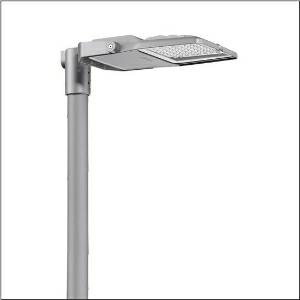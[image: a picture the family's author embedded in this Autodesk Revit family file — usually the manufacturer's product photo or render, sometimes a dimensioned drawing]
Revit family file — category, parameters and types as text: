
# Revit family: floodlight_fl_21_iq_mini___pl61_5xa7772b2c3a_0206
name_source: partatom
category: Lighting Fixtures
units: mm (PartAtom-declared; Revit-internal decimal feet)

## family parameters
Cut with Voids When Loaded = No
Host = Face
Light Source = No
Part Type = Normal
Room Calculation Point = No
Round Connector Dimension = Use Diameter
Shared = No

## types (1)
- --- (1 x LED, 6120 lm, 45.5 W, 3000K)
    Apparent Load = 46 VA
    CIE Flux Codes = 33 65 98 100 100
    Color Rendering = 70
    Color Temperature = 3000K
    Default Elevation = 1800 mm
    Description = Floodlight FL 21 iQ mini, floodlight, primary light control with lens, of PMMA, primary optical cover: protective disc, of toughened safety glass, transparent, light distribution: PL61, light emission: direct distribution, installation type: surface-mounted, LED, High Power LED, rated luminous flux: 6.120lm, luminous efficacy: 135lm/W, light colour: 730, colour temperature: 3000K, control gear: iQ Street-Remote/DALI, control: Auto-Match, Temp-Guard, Night-Set, Smart-Wire, Desk-Remote (wireless, voltage-free reading and setting of iQ features in the workshop via application-optimized NFC function/RFID function), optimised constant luminous flux control (CLO 2.0), Light-Fading, Lumen-Switch, with terminal, 6-pole, mains connection: 220..240V, AC, 50/60Hz, start of lifetime: 46W, end of service life: 48W, reduction: 22W, luminaire housing, of diecast aluminium, powder-coated, Siteco® metallic grey (DB 702S), corrosivity category C5 mid according to DIN EN ISO 12944, suitable for swimming pools, chlorine-resistant, sealing non-destructively replaceable, please order mast flange separately, mast bracket, of steel, galvanised, powder-coated, protection rating (complete): IP66, insulation class (complete): insulation class II (safety insulation), certification: CE, ENEC, VDE, protection symbol: D, impact resistance: IK08, permissible operating ambient temperature: -40..+40°C, permissible operating ambient temperature for outdoor applications: -40..+50°C, standard: DIN EN 12944, LABS conformity tested according to VDMA 24364:2018-05, packaging unit: 1 piece

Light Distribution: PL61
    Height = 70 mm
    Lamp = 1 x LED
    Lamp Light Flux = 6120 lm
    Lamp Power = 45.5 W
    Lamp count = 1
    Length = 485 mm
    Luminous efficacy = 135 lm/W
    Manufacturer = Siteco
    ModVariant = No
    Model = 5XA7772B2C3A
    Number of Poles = 1
    OnlyDefault = Yes
    Power Factor = 1
    Product Name = Floodlight FL 21 iQ mini | PL61
    Product group = floodlight | pylon annexe
    ProductGroupID = 6200
    Protection Class = Protection class II
    Protection Degree = IP 66
    RLX_Detail_Level = 1
    RLX_Emergency_Light_Flux = 0 lm
    RLX_Emergency_Type = 0
    RLX_Emergency_Type_DB = No
    RlxData = <blob elided: 101261 chars, md5=3218f21f>
    Socket = socket
    Standby Power = 0 W
    System Light Flux = 6120 lm
    System Power = 46 W
    Type Comments = factory setting: luminous flux: 100 % | dim-lin: 254 | 463 mA
    Type Image = l_1007125.jpg
    URL = http://relux.com
    VarID = @adj_173584
    Voltage = 0 V
    Weight = 0.00 kg
    Width = 337 mm

## geometry (parser evidence)
native form markers: Blend x4, Sweep x12
no freeform markers — native parametric forms only
